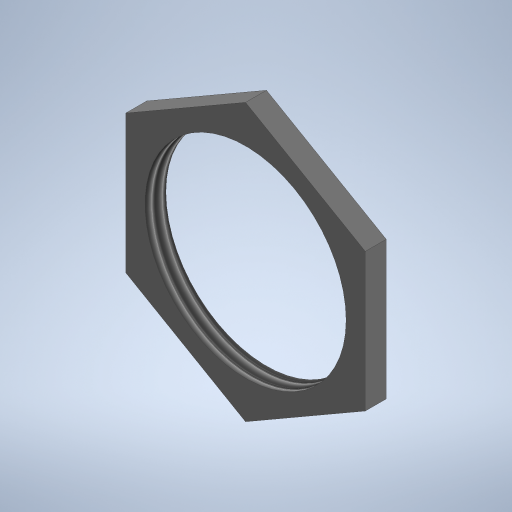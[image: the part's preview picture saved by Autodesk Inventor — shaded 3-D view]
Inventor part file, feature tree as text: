
AUTODESK INVENTOR PART (.ipt)
format: ipt  version: 2023 (Build 270158000, 158)  size: 252,416 bytes
history: native  units: in
note: dims shown in document units (in); Inventor stores cm internally (conversion verified against a paired STEP export)
features: sketch x2, extrude x1, hole x1
ambient origin geometry x8: Origin, YZ Plane, XZ Plane, XY Plane, X Axis, Y Axis, Z Axis, Center Point
bodies: Solid1 (feature_tree)
feature tree (4):
  extrude  "Extrusion1"  Depth=0.0984in TaperAngle=0.0deg
  hole  "Hole1"  [1 undecoded]
  sketch  "Sketch1"  dims[d0=1.126in d1=0.0984in d2=0.0in]
  sketch  "Sketch2"  dims[d3=0.946in d4=2.0in d5=0.1575in d6=0.0787in d7=90.0deg d8=0.315in d9=0.8108in]
note: 1 required parameter value undecoded (feature->parameter linkage not recoverable at this tier; creation-order binding heuristic only, values carry confidence <= 0.55)
